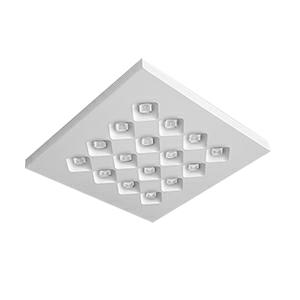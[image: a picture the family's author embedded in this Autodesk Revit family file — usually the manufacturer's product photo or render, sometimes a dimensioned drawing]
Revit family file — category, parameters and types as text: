
# Revit family: 3f_filippi_-_3f_diagon_3f_filippi_-_23026_a0686_-_3f_diagon_25w-840_596x596___corn_plaf__d6cb
name_source: partatom
category: Lighting Fixtures
units: mm (PartAtom-declared; Revit-internal decimal feet)

## family parameters
Cut with Voids When Loaded = No
Host = Face
Light Source = No
Part Type = Normal
Room Calculation Point = No
Round Connector Dimension = Use Diameter
Shared = No

## types (1)
- 3F Filippi - 3F Dìagon (1 x LED, 4250 lm, 28 W, 4000 K)
    Apparent Load = 28 VA
    Approval mark = CE
    CIE Flux Codes = 67 96 100 100 100
    Color Rendering = 80
    Color Temperature = 4000 K
    Control Gear = Electronic ballast
    Default Elevation = 1800 mm
    Description = ILLUMINOTECHNICAL
Luminous efficiency 100% (DLOR 100%, ULOR 0%).
Initial luminous flux of the luminaire 4250 lm.
Direct symmetric distribution.
Installation Interdistance Transv.D = 1.39 x hu - Long.D = 1.39 x hu.
Average luminance <1500 cd/m² for radial angles >65°.
Tabular UGR (CIE 117 - 4H-8H; S=0.25H; 70/50/20): RUG 17.3 - 17.3.
Beam angle: 93° - 92°.
Luminous efficacy 152 lm/W.
Lifetime (L95/B10): 30000 h. (tq+25°C)
Lifetime (L90/B10): 50000 h. (tq+25°C)
Lifetime (L80/B10): 80000 h. (tq+25°C)
Lifetime (L75/B10): 100000 h. (tq+25°C)
Sudden decreased luminous flux after 50000 hours: 0% (C0).
Photobiological safety in compliance with IEC/TR 62778: RG0 risk exempt, (IEC 62471).
In compliance with IEC/EN 62722-2-1 - IEC/EN 62717 standards.

SOURCE
Squared LED module 25W/840.
Energy efficiency class (UE 2019/2020 - UE 2019/2015): C.
CIE 13.3 Colour rendering index: CRI >80 (R9 <50%).
IES TM-30 Fidelity Index: Rf = 84 Rg = 95.
CCT nominal colour temperature 4000 K.
Colour initial tolerance (MacAdam): SDCM 3.

MECHANICAL
Housing in hot-galvanised steel, painted in white polyester.
Honeycombed diagonal screen in white anti-glare polycarbonate.
Rhomboidal lenses with differentiated surfaces, etched and prismatic to optimise the orientation of the luminous flux, in transparent methacrylate (PMMA).
Luminaire with limited surface temperature. - D - (EN 60598-2-24)
Dimensions: 600x600 mm, height 40 mm. Weight 6.205 kg.
IP43 protection degree for exposed part, IP20 for recessed part.
Mechanical strength to impacts IK06 (1 joule).
Glow-wire test resistance 650°C.

ELECTRICAL
Halogen Free electronic wiring 230V-50/60Hz, power factor 0.95, THD <25%, constant output current, class I, 1 driver.
Power of the luminaire 28 W.
ENEC - CE.
SAFE FLICKER: PstLM=<1 and SVM=<0.4 (IEC TR 61547-1 and IEC TR 63158), to ensure a more comfortable and safe light.
Luminaire compliant with EN 60598-2-22 for power supply from a centralised emergency system CPSS (Central Power Supply System), not incorporated in the luminaire - high risk areas excluded. The default power and flux are 100% in AC and 100% in DC.
Ambient temperature from 0°C to +25°C.
Temperature class T6 max 85°C.
Quick connection.
Relative humidity UR: <85%.

INSTALLATION
Ceiling.
Height only 40 mm.
All accessories dedicated to this product are available on the Catalog and on our website www.3F-Filippi.com.

ACCESSORIES
A0686 - 596x596 Diagon frame for Ceiling installation.

APPLICATIONS
Environments: staterooms, with VDTs, offices.
Environments with exacting visual tasks, where diffused soft light for optimum visual comfort is required.

WARNING
Luminaire designed for disposal/recycling at end-of-life.
Replaceable (LED only) light source by a professional. Replaceable control gear by a professional.
    Height = 0 mm  [stored 0 ft]
    Lamp = 1 x LED
    Lamp Light Flux = 4250 lm
    Lamp Power = 28 W
    Lamp count = 1
    Length = 600 mm
    Lifetime = 50000 h
    Luminous efficacy = 152 lm/W
    Manufacturer = 3F Filippi
    ModVariant = No
    Model = 3F Filippi - 23026+A0686 - 3F Diagon 25W-840 596x596 + Corn.plaf.
    Mounting Place = Ceiling
    Mounting Type = Recessed
    Number of Poles = 1
    OnlyDefault = Yes
    Power Factor = 1
    Product Name = 3F Filippi - 3F Dìagon
    Product group = recessed luminaire
    ProductGroupID = 4
    Protection Class = Protection class I
    Protection Degree = IP 20
    RLX_Detail_Level = 1
    RLX_Emergency_Light_Flux = 0 lm
    RLX_Emergency_Type = 0
    RLX_Emergency_Type_DB = No
    RlxData = <blob elided: 96189 chars, md5=219ea3c4>
    Socket = socket
    Standby Power = 0 W
    System Light Flux = 4250 lm
    System Power = 28 W
    Type Comments = Product without accessories
    Type Image = 3ffilippi_3f_diagon__a0686.jpg
    URL = http://relux.com
    VarID = ---
    Voltage = 0 V
    Weight = 0.00 kg
    Width = 600 mm

note: [stored X ft] marks values corroborated as IEEE doubles in the binary element streams (Revit-internal decimal feet)

## geometry (parser evidence)
native form markers: Blend x4, Sweep x8
no freeform markers — native parametric forms only
